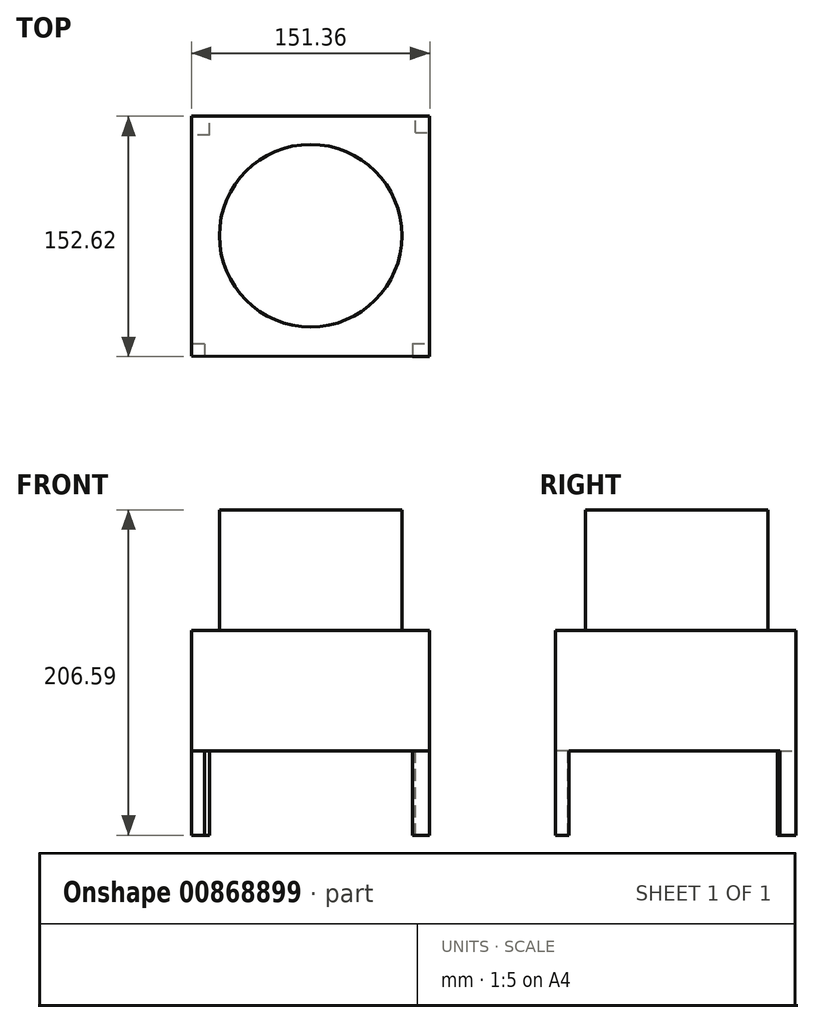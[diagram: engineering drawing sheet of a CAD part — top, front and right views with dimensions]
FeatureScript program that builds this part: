
annotation { "Feature Type Name" : "Feature", "Feature Type Description" : "" }
export const myFeature = defineFeature(function(context is Context, id is Id, definition is map)
    precondition{}
    {
        {
            var Q0;
            Q0=qCreatedBy(makeId("Top.planeOp"),FACE);
            var sketch = newSketch(context, id + "F0", { "sketchPlane" : qUnion([Q0])});
            skCircle(sketch, "E0", {"center": v(0, 0) * mm, "radius": 57.97 * mm});
            skSolve(sketch);
        }
        {
            var Q0;
            Q0 = qSketchRegion(id + "F0", true);
            extrude(context, id + "F1", {"entities" : qUnion([Q0]), "depth" : 76.56 * mm, "offsetDistance" : 25.4 * mm});
        }
        {
            var Q0;
            Q0=qCreatedBy(makeId("Top.planeOp"),FACE);
            var sketch = newSketch(context, id + "F2", { "sketchPlane" : qUnion([Q0])});
            skLineSegment(sketch, "E1", {"start": v(75.64, -76.76) * mm, "end": v(75.64, 75.86) * mm});
            skLineSegment(sketch, "E2", {"start": v(75.64, 75.86) * mm, "end": v(-75.72, 75.86) * mm});
            skLineSegment(sketch, "E3", {"start": v(-75.72, 75.86) * mm, "end": v(-75.72, -76.58) * mm});
            skLineSegment(sketch, "E4", {"start": v(-75.72, -76.58) * mm, "end": v(75.64, -76.76) * mm});
            skSolve(sketch);
        }
        {
            var Q0;
            Q0 = qSketchRegion(id + "F2", true);
            extrude(context, id + "F3", {"entities" : qUnion([Q0]), "operationType" : NewBodyOperationType.ADD, "oppositeDirection" : true, "depth" : 76.5 * mm, "offsetDistance" : 25.4 * mm});
        }
        {
            var Q0;
            Q0=makeQuery(id+"F3.opExtrude","CAP_FACE",FACE,{"disambiguationData":[OSD([sQuery(id+"F2.wireOp",EDGE,"E1"),sQuery(id+"F2.wireOp",EDGE,"E2"),sQuery(id+"F2.wireOp",EDGE,"E3"),sQuery(id+"F2.wireOp",EDGE,"E4")])],"isStart":false});
            var sketch = newSketch(context, id + "F4", { "sketchPlane" : qUnion([Q0])});
            skLineSegment(sketch, "E5.bottom", {"start": v(-64.29, -63.93) * mm, "end": v(-75.72, -63.93) * mm});
            skLineSegment(sketch, "E5.top", {"start": v(-64.29, -75.86) * mm, "end": v(-75.72, -75.86) * mm});
            skLineSegment(sketch, "E5.left", {"start": v(-64.29, -63.93) * mm, "end": v(-64.29, -75.86) * mm});
            skLineSegment(sketch, "E5.right", {"start": v(-75.72, -63.93) * mm, "end": v(-75.72, -75.86) * mm});
            skLineSegment(sketch, "E6.bottom", {"start": v(66.51, -65.63) * mm, "end": v(75.64, -65.63) * mm});
            skLineSegment(sketch, "E6.top", {"start": v(66.51, -75.86) * mm, "end": v(75.64, -75.86) * mm});
            skLineSegment(sketch, "E6.left", {"start": v(66.51, -65.63) * mm, "end": v(66.51, -75.86) * mm});
            skLineSegment(sketch, "E6.right", {"start": v(75.64, -65.63) * mm, "end": v(75.64, -75.86) * mm});
            skLineSegment(sketch, "E7.bottom", {"start": v(64.7, 68.49) * mm, "end": v(75.64, 68.49) * mm});
            skLineSegment(sketch, "E7.top", {"start": v(64.7, 76.76) * mm, "end": v(75.64, 76.76) * mm});
            skLineSegment(sketch, "E7.left", {"start": v(64.7, 68.49) * mm, "end": v(64.7, 76.76) * mm});
            skLineSegment(sketch, "E7.right", {"start": v(75.64, 68.49) * mm, "end": v(75.64, 76.76) * mm});
            skLineSegment(sketch, "E8.bottom", {"start": v(-67.31, 68.97) * mm, "end": v(-75.72, 68.97) * mm});
            skLineSegment(sketch, "E8.top", {"start": v(-67.31, 76.58) * mm, "end": v(-75.72, 76.58) * mm});
            skLineSegment(sketch, "E8.left", {"start": v(-67.31, 68.97) * mm, "end": v(-67.31, 76.58) * mm});
            skLineSegment(sketch, "E8.right", {"start": v(-75.72, 68.97) * mm, "end": v(-75.72, 76.58) * mm});
            skSolve(sketch);
        }
        {
            var Q0;
            Q0 = qSketchRegion(id + "F4", true);
            extrude(context, id + "F5", {"entities" : qUnion([Q0]), "operationType" : NewBodyOperationType.ADD, "depth" : 53.52 * mm, "offsetDistance" : 25.4 * mm});
        }
    });
